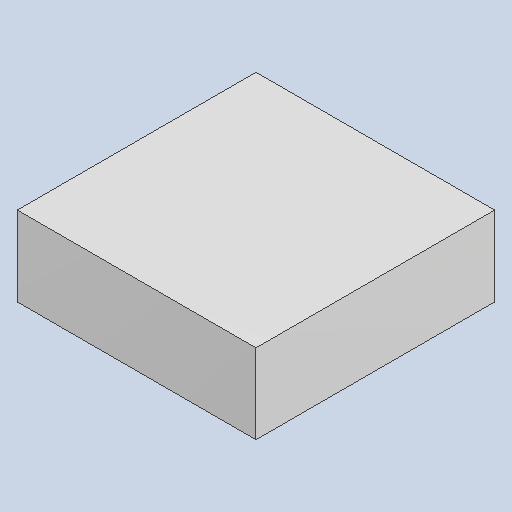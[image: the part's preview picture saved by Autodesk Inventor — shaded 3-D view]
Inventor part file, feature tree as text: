
AUTODESK INVENTOR PART (.ipt)
format: ipt  version: 2023.4 (Build 274418000, 418)  size: 79,872 bytes
history: native  units: mm
features: extrude x1
ambient origin geometry x8: Origin, YZ Plane, XZ Plane, XY Plane, X Axis, Y Axis, Z Axis, Center Point
bodies: Solid1 (feature_tree)
feature tree (1):
  extrude  "Extruded_2"  [1 undecoded]
note: 1 required parameter value undecoded (feature->parameter linkage not recoverable at this tier; creation-order binding heuristic only, values carry confidence <= 0.55)
